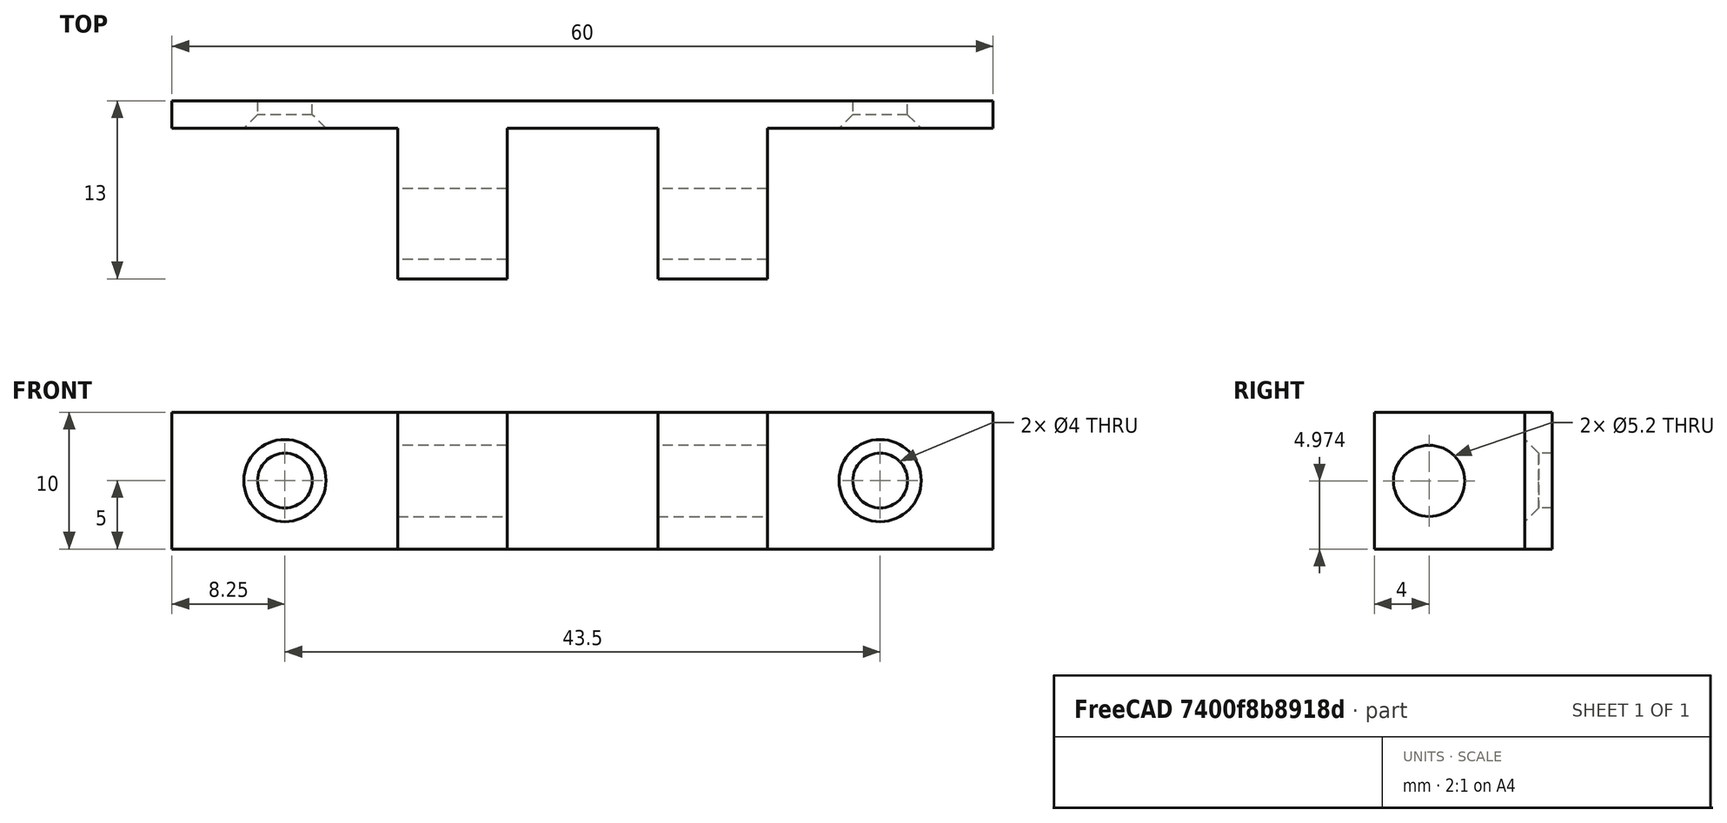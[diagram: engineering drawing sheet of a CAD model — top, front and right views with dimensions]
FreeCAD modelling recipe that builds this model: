
FCSTD DOCUMENT  (FreeCAD 0.20R29410 (Git))
Label: frameFixationShort
License: All rights reserved
LicenseURL: http://en.wikipedia.org/wiki/All_rights_reserved
objects: TechDraw::DrawViewDimension×12, Sketcher::SketchObject×5, PartDesign::Pocket×3, TechDraw::DrawProjGroupItem×3, PartDesign::Pad×2, PartDesign::Chamfer×1, PartDesign::Body×1, TechDraw::DrawSVGTemplate×1, TechDraw::DrawProjGroup×1, TechDraw::DrawPage×1
note: 18 computed .brp shape members not serialized (recipe doc carries the construction recipe); baked Part::Feature solids carry a one-line shape summary decoded from their .brp

FEATURE [Sketcher::SketchObject] Sketch
  FullyConstrained = true
  MapMode = 5
  Placement = pos=(0,0,0) rot=(1,0,0;1.5708rad)
  Support = -> [XZ_Plane]
  sketch-geometry (4):
    g0: LineSegment StartX=0 StartY=0 StartZ=0 EndX=60 EndY=0 EndZ=0
    g1: LineSegment StartX=0 StartY=50 StartZ=0 EndX=60 EndY=50 EndZ=0
    g2: LineSegment StartX=0 StartY=0 StartZ=0 EndX=0 EndY=50 EndZ=0
    g3: LineSegment StartX=60 StartY=50 StartZ=0 EndX=60 EndY=0 EndZ=0
  constraints (11):
    c: Coincident(g0,g-1)
    c: PointOnObject(g0,g-1)
    c: Distance(g0) = 60
    c: PointOnObject(g1,g-2)
    c: Horizontal(g1)
    c: Equal(g0,g1)
    c: DistanceY(g0,g1) = 50
    c: Coincident(g2,g0)
    c: Coincident(g2,g1)
    c: Coincident(g3,g1)
    c: Coincident(g3,g0)
FEATURE [PartDesign::Pad] Pad
  Direction = (1,1,1)
  Length = 2
  Length2 = 100
  Placement = pos=(0,0,0) rot=(1,0,0;1.5708rad)
  Profile = -> Sketch
  Type = 0
FEATURE [Sketcher::SketchObject] Sketch001
  FullyConstrained = true
  MapMode = 5
  Placement = pos=(0,-2,0) rot=(1,0,0;1.5708rad)
  Support = -> [Pad]
  sketch-geometry (8):
    g0: LineSegment StartX=16.5 StartY=0 StartZ=0 EndX=24.5 EndY=0 EndZ=0
    g1: LineSegment StartX=35.5 StartY=0 StartZ=0 EndX=43.5 EndY=0 EndZ=0
    g2: LineSegment StartX=16.5 StartY=0 StartZ=0 EndX=16.5 EndY=10 EndZ=0
    g3: LineSegment StartX=24.5 StartY=0 StartZ=0 EndX=24.5 EndY=10 EndZ=0
    g4: LineSegment StartX=35.5 StartY=0 StartZ=0 EndX=35.5 EndY=10 EndZ=0
    g5: LineSegment StartX=43.5 StartY=0 StartZ=0 EndX=43.5 EndY=10 EndZ=0
    g6: LineSegment StartX=16.5 StartY=10 StartZ=0 EndX=24.5 EndY=10 EndZ=0
    g7: LineSegment StartX=35.5 StartY=10 StartZ=0 EndX=43.5 EndY=10 EndZ=0
  constraints (24):
    c: PointOnObject(g0,g-1)
    c: PointOnObject(g0,g-1)
    c: Distance(g0) = 8
    c: DistanceX(g-1,g0) = 24.5
    c: PointOnObject(g1,g-1)
    c: PointOnObject(g1,g-1)
    c: Equal(g0,g1)
    c: DistanceX(g0,g1) = 11
    c: Coincident(g2,g0)
    c: Vertical(g2)
    c: Distance(g2) = 10
    c: Coincident(g3,g0)
    c: Vertical(g3)
    c: Coincident(g4,g1)
    c: Coincident(g5,g1)
    c: Vertical(g5)
    c: Equal(g2,g3)
    c: Equal(g3,g4)
    c: Equal(g4,g5)
    c: Vertical(g4)
    c: Coincident(g6,g2)
    c: Coincident(g6,g3)
    c: Coincident(g7,g4)
    c: Coincident(g7,g5)
FEATURE [PartDesign::Pad] Pad001
  BaseFeature = -> Pad
  Direction = (1,1,1)
  Length = 11
  Length2 = 100
  Placement = pos=(0,0,0) rot=(1,0,0;1.5708rad)
  Profile = -> Sketch001
  Type = 0
FEATURE [Sketcher::SketchObject] Sketch002
  FullyConstrained = false
  MapMode = 5
  Placement = pos=(16.5,0,0) rot=(0.707107,0,-0.707107;3.14159rad)
  Support = -> [Pad001]
  sketch-geometry (1):
    g0: Circle CenterX=-4.9743 CenterY=9 CenterZ=0 NormalX=0 NormalY=0 NormalZ=1 AngleXU=0 Radius=2.6
  constraints (2):
    c: Diameter(g0) = 5.2
    c: DistanceY(g-1,g0) = 9
FEATURE [PartDesign::Pocket] Pocket
  BaseFeature = -> Pad001
  Direction = (1,1,1)
  Length = 5
  Length2 = 100
  Placement = pos=(0,0,0) rot=(1,0,0;1.5708rad)
  Profile = -> Sketch002
  Type = 1
FEATURE [Sketcher::SketchObject] Sketch003
  ExternalGeometry = -> [Pocket]
  FullyConstrained = true
  MapMode = 5
  Placement = pos=(0,-2,0) rot=(1,0,0;1.5708rad)
  Support = -> [Pocket]
  sketch-geometry (4):
    g0: LineSegment StartX=0 StartY=50 StartZ=0 EndX=0 EndY=10 EndZ=0
    g1: LineSegment StartX=0 StartY=50 StartZ=0 EndX=60 EndY=50 EndZ=0
    g2: LineSegment StartX=60 StartY=50 StartZ=0 EndX=60 EndY=10 EndZ=0
    g3: LineSegment StartX=0 StartY=10 StartZ=0 EndX=60 EndY=10 EndZ=0
  constraints (10):
    c: Coincident(g0,g-4)
    c: PointOnObject(g0,g-4)
    c: Coincident(g1,g0)
    c: Coincident(g1,g-5)
    c: Coincident(g2,g1)
    c: PointOnObject(g2,g-5)
    c: Coincident(g3,g0)
    c: Coincident(g3,g2)
    c: Horizontal(g3)
    c: PointOnObject(g-6,g3)
FEATURE [PartDesign::Pocket] Pocket001
  BaseFeature = -> Pocket
  Direction = (0,1,-2e-16)
  Length = 5
  Length2 = 5
  Placement = pos=(0,0,0) rot=(1,0,0;1.5708rad)
  Profile = -> Sketch003
  ReferenceAxis = -> Sketch003 [N_Axis]
  Type = 1
FEATURE [Sketcher::SketchObject] Sketch004
  ExternalGeometry = -> [Pocket001]
  FullyConstrained = true
  MapMode = 5
  Placement = pos=(0,-2,0) rot=(1,0,0;1.5708rad)
  Support = -> [Pocket001]
  sketch-geometry (10):
    g0: Circle CenterX=8.25 CenterY=5 CenterZ=0 NormalX=0 NormalY=0 NormalZ=1 AngleXU=0 Radius=2
    g1: Circle CenterX=51.75 CenterY=5 CenterZ=0 NormalX=0 NormalY=0 NormalZ=1 AngleXU=0 Radius=2
    g2: LineSegment StartX=8.25 StartY=5 StartZ=0 EndX=0 EndY=5 EndZ=0
    g3: LineSegment StartX=8.25 StartY=5 StartZ=0 EndX=16.5 EndY=5 EndZ=0
    g4: LineSegment StartX=8.25 StartY=5 StartZ=0 EndX=8.25 EndY=10 EndZ=0
    g5: LineSegment StartX=8.25 StartY=5 StartZ=0 EndX=8.25 EndY=0 EndZ=0
    g6: LineSegment StartX=51.75 StartY=5 StartZ=0 EndX=43.5 EndY=5 EndZ=0
    g7: LineSegment StartX=51.75 StartY=5 StartZ=0 EndX=60 EndY=5 EndZ=0
    g8: LineSegment StartX=51.75 StartY=4e-16 StartZ=0 EndX=51.75 EndY=5 EndZ=0
    g9: LineSegment StartX=51.75 StartY=5 StartZ=0 EndX=51.75 EndY=10 EndZ=0
  constraints (30):
    c: Diameter(g0) = 4
    c: Diameter(g1) = 4
    c: Coincident(g2,g0)
    c: PointOnObject(g2,g-4)
    c: Horizontal(g2)
    c: Coincident(g3,g0)
    c: PointOnObject(g3,g-9)
    c: Horizontal(g3)
    c: Coincident(g4,g0)
    c: PointOnObject(g4,g-3)
    c: Vertical(g4)
    c: Coincident(g5,g0)
    c: PointOnObject(g5,g-5)
    c: Vertical(g5)
    c: Equal(g2,g3)
    c: Equal(g5,g4)
    c: Coincident(g6,g1)
    c: PointOnObject(g6,g-10)
    c: Coincident(g7,g1)
    c: PointOnObject(g7,g-7)
    c: Horizontal(g7)
    c: PointOnObject(g8,g-8)
    c: Coincident(g8,g1)
    c: Coincident(g9,g1)
    c: PointOnObject(g9,g-6)
    c: Equal(g6,g7)
    c: Horizontal(g6)
    c: Equal(g9,g8)
    c: Vertical(g9)
    c: Vertical(g8)
FEATURE [PartDesign::Pocket] Pocket002
  BaseFeature = -> Pocket001
  Direction = (0,1,-2e-16)
  Length = 5
  Length2 = 5
  Placement = pos=(0,0,0) rot=(1,0,0;1.5708rad)
  Profile = -> Sketch004
  ReferenceAxis = -> Sketch004 [N_Axis]
  Type = 1
FEATURE [PartDesign::Chamfer] Chamfer
  Angle = 45
  Base = -> Pocket002 [Edge18,Edge26]
  BaseFeature = -> Pocket002
  ChamferType = 0
  FlipDirection = false
  Placement = pos=(0,0,0) rot=(1,0,0;1.5708rad)
  Size = 1
  Size2 = 1
  SupportTransform = false
  UseAllEdges = false
FEATURE [PartDesign::Body] Body
  Group = -> [Sketch,Pad,Sketch001,Pad001,Sketch002,Pocket,Sketch003,Pocket001,Sketch004,Pocket002,Chamfer]
  Origin = -> Origin
  Tip = -> Chamfer
FEATURE [TechDraw::DrawSVGTemplate] Template
  EditableTexts = Designed_by_Name=Белкин Никита; FC-Date=16.04.2023; FC-SC=2:1; FC-Title=Крепление к раме(уменьш.)
  Height = 210
  Orientation = 1
  Width = 297
FEATURE [TechDraw::DrawProjGroupItem] ProjItem  label="Front"
  CoarseView = false
  Direction = (1,0,0)
  Focus = 100
  HardHidden = false
  IsoCount = 0
  IsoHidden = false
  IsoVisible = false
  LockPosition = true
  Perspective = false
  Rotation = 0
  RotationVector = (0,0,1)
  Scale = 2
  ScaleType = 2
  SeamHidden = false
  SeamVisible = true
  SmoothHidden = false
  SmoothVisible = true
  Source = -> [Body]
  Type = 0
  X = 0
  XDirection = (0,0,1)
  Y = 0
FEATURE [TechDraw::DrawProjGroupItem] ProjItem002  label="Left"
  CoarseView = false
  Direction = (1e-16,0,-1)
  Focus = 100
  HardHidden = false
  IsoCount = 0
  IsoHidden = false
  IsoVisible = false
  LockPosition = false
  Perspective = false
  Rotation = 0
  RotationVector = (1,0,0)
  ScaleType = 2
  SeamHidden = false
  SeamVisible = true
  SmoothHidden = false
  SmoothVisible = true
  Source = -> [Body]
  Type = 1
  X = 135
  XDirection = (1,0,1e-16)
  Y = 0
FEATURE [TechDraw::DrawProjGroupItem] ProjItem003  label="Top"
  CoarseView = false
  Direction = (0,-1,0)
  Focus = 100
  HardHidden = false
  IsoCount = 0
  IsoHidden = false
  IsoVisible = false
  LockPosition = false
  Perspective = false
  Rotation = 0
  RotationVector = (1,0,0)
  ScaleType = 2
  SeamHidden = false
  SeamVisible = true
  SmoothHidden = false
  SmoothVisible = true
  Source = -> [Body]
  Type = 4
  X = 0
  XDirection = (0,0,1)
  Y = -88.1988
FEATURE [TechDraw::DrawProjGroup] ProjGroup
  Anchor = -> ProjItem
  AutoDistribute = true
  LockPosition = false
  ProjectionType = 0
  Rotation = 0
  Scale = 2
  ScaleType = 2
  Source = -> [Body]
  Views = -> [ProjItem,ProjItem002,ProjItem003]
  X = 64.3768
  Y = 169.444
  spacingX = 15
  spacingY = 15
FEATURE [TechDraw::DrawViewDimension] Dimension
  AngleOverride = false
  Arbitrary = false
  ArbitraryTolerances = false
  EqualTolerance = true
  ExtensionAngle = 0
  FormatSpec = %.2w
  FormatSpecOverTolerance = %+.2w
  FormatSpecUnderTolerance = %+.2w
  Inverted = false
  LineAngle = 0
  LockPosition = false
  MeasureType = 1
  OverTolerance = 0
  References2D = -> [ProjItem]
  Rotation = 0
  ScaleType = 0
  TheoreticalExact = false
  Type = 1
  UnderTolerance = 0
  X = -0.746894
  Y = 26.718
FEATURE [TechDraw::DrawViewDimension] Dimension001
  AngleOverride = false
  Arbitrary = false
  ArbitraryTolerances = false
  EqualTolerance = true
  ExtensionAngle = 0
  FormatSpec = ⌀%.2w
  FormatSpecOverTolerance = %+.2w
  FormatSpecUnderTolerance = %+.2w
  Inverted = false
  LineAngle = 0
  LockPosition = false
  MeasureType = 1
  OverTolerance = 0
  References2D = -> [ProjItem]
  Rotation = 0
  ScaleType = 0
  TheoreticalExact = false
  Type = 5
  UnderTolerance = 0
  X = -25.3944
  Y = 25.021
FEATURE [TechDraw::DrawViewDimension] Dimension002
  AngleOverride = false
  Arbitrary = false
  ArbitraryTolerances = false
  EqualTolerance = true
  ExtensionAngle = 0
  FormatSpec = %.2w
  FormatSpecOverTolerance = %+.2w
  FormatSpecUnderTolerance = %+.2w
  Inverted = false
  LineAngle = 0
  LockPosition = false
  MeasureType = 1
  OverTolerance = 0
  References2D = -> [ProjItem]
  Rotation = 0
  ScaleType = 0
  TheoreticalExact = false
  Type = 2
  UnderTolerance = 0
  X = -25.6848
  Y = 4.14114
FEATURE [TechDraw::DrawViewDimension] Dimension003
  AngleOverride = false
  Arbitrary = false
  ArbitraryTolerances = false
  EqualTolerance = true
  ExtensionAngle = 0
  FormatSpec = %.2w
  FormatSpecOverTolerance = %+.2w
  FormatSpecUnderTolerance = %+.2w
  Inverted = false
  LineAngle = 0
  LockPosition = false
  MeasureType = 1
  OverTolerance = 0
  References2D = -> [ProjItem]
  Rotation = 0
  ScaleType = 0
  TheoreticalExact = false
  Type = 2
  UnderTolerance = 0
  X = -21.3439
  Y = -19.0073
FEATURE [TechDraw::DrawViewDimension] Dimension004
  AngleOverride = false
  Arbitrary = false
  ArbitraryTolerances = false
  EqualTolerance = true
  ExtensionAngle = 0
  FormatSpec = %.2w
  FormatSpecOverTolerance = %+.2w
  FormatSpecUnderTolerance = %+.2w
  Inverted = false
  LineAngle = 0
  LockPosition = false
  MeasureType = 1
  OverTolerance = 0
  References2D = -> [ProjItem002]
  Rotation = 0
  ScaleType = 0
  TheoreticalExact = false
  Type = 1
  UnderTolerance = 0
  X = -19.2161
  Y = 25.8881
FEATURE [TechDraw::DrawViewDimension] Dimension005
  AngleOverride = false
  Arbitrary = false
  ArbitraryTolerances = false
  EqualTolerance = true
  ExtensionAngle = 0
  FormatSpec = %.2w
  FormatSpecOverTolerance = %+.2w
  FormatSpecUnderTolerance = %+.2w
  Inverted = false
  LineAngle = 0
  LockPosition = false
  MeasureType = 1
  OverTolerance = 0
  References2D = -> [ProjItem002]
  Rotation = 0
  ScaleType = 0
  TheoreticalExact = false
  Type = 1
  UnderTolerance = 0
  X = 18.3517
  Y = 25.8788
FEATURE [TechDraw::DrawViewDimension] Dimension006
  AngleOverride = false
  Arbitrary = false
  ArbitraryTolerances = false
  EqualTolerance = true
  ExtensionAngle = 0
  FormatSpec = %.2w
  FormatSpecOverTolerance = %+.2w
  FormatSpecUnderTolerance = %+.2w
  Inverted = false
  LineAngle = 0
  LockPosition = false
  MeasureType = 1
  OverTolerance = 0
  References2D = -> [ProjItem002]
  Rotation = 0
  ScaleType = 0
  TheoreticalExact = false
  Type = 1
  UnderTolerance = 0
  X = -0.58037
  Y = -24.0083
FEATURE [TechDraw::DrawViewDimension] Dimension007
  AngleOverride = false
  Arbitrary = false
  ArbitraryTolerances = false
  EqualTolerance = true
  ExtensionAngle = 0
  FormatSpec = %.2w
  FormatSpecOverTolerance = %+.2w
  FormatSpecUnderTolerance = %+.2w
  Inverted = false
  LineAngle = 0
  LockPosition = false
  MeasureType = 1
  OverTolerance = 0
  References2D = -> [ProjItem002]
  Rotation = 0
  ScaleType = 0
  TheoreticalExact = false
  Type = 1
  UnderTolerance = 0
  X = -0.822022
  Y = 25.9023
FEATURE [TechDraw::DrawViewDimension] Dimension008
  AngleOverride = false
  Arbitrary = false
  ArbitraryTolerances = false
  EqualTolerance = true
  ExtensionAngle = 0
  FormatSpec = ⌀%.2w
  FormatSpecOverTolerance = %+.2w
  FormatSpecUnderTolerance = %+.2w
  Inverted = false
  LineAngle = 0
  LockPosition = false
  MeasureType = 1
  OverTolerance = 0
  References2D = -> [ProjItem003]
  Rotation = 0
  ScaleType = 0
  TheoreticalExact = false
  Type = 5
  UnderTolerance = 0
  X = -20.3598
  Y = -27.9356
FEATURE [TechDraw::DrawViewDimension] Dimension009
  AngleOverride = false
  Arbitrary = false
  ArbitraryTolerances = false
  EqualTolerance = true
  ExtensionAngle = 0
  FormatSpec = ⌀%.2w
  FormatSpecOverTolerance = %+.2w
  FormatSpecUnderTolerance = %+.2w
  Inverted = false
  LineAngle = 0
  LockPosition = false
  MeasureType = 1
  OverTolerance = 0
  References2D = -> [ProjItem003]
  Rotation = 0
  ScaleType = 0
  TheoreticalExact = false
  Type = 5
  UnderTolerance = 0
  X = -25.3314
  Y = -37.4053
FEATURE [TechDraw::DrawViewDimension] Dimension010
  AngleOverride = false
  Arbitrary = false
  ArbitraryTolerances = false
  EqualTolerance = true
  ExtensionAngle = 0
  FormatSpec = %.2w
  FormatSpecOverTolerance = %+.2w
  FormatSpecUnderTolerance = %+.2w
  Inverted = false
  LineAngle = 0
  LockPosition = false
  MeasureType = 1
  OverTolerance = 0
  References2D = -> [ProjItem002]
  Rotation = 0
  ScaleType = 0
  TheoreticalExact = false
  Type = 1
  UnderTolerance = 0
  X = -44.3523
  Y = 25.9009
FEATURE [TechDraw::DrawViewDimension] Dimension011
  AngleOverride = false
  Arbitrary = false
  ArbitraryTolerances = false
  EqualTolerance = true
  ExtensionAngle = 0
  FormatSpec = %.2w
  FormatSpecOverTolerance = %+.2w
  FormatSpecUnderTolerance = %+.2w
  Inverted = false
  LineAngle = 0
  LockPosition = false
  MeasureType = 1
  OverTolerance = 0
  References2D = -> [ProjItem002]
  Rotation = 0
  ScaleType = 0
  TheoreticalExact = false
  Type = 1
  UnderTolerance = 0
  X = 43.5
  Y = 25.9009
FEATURE [TechDraw::DrawPage] Page
  KeepUpdated = true
  NextBalloonIndex = 1
  ProjectionType = 0
  Template = -> Template
  Views = -> [ProjGroup,Dimension,Dimension001,Dimension002,Dimension003,Dimension004,Dimension005,Dimension006,Dimension007,Dimension008,Dimension009,Dimension010,Dimension011]
